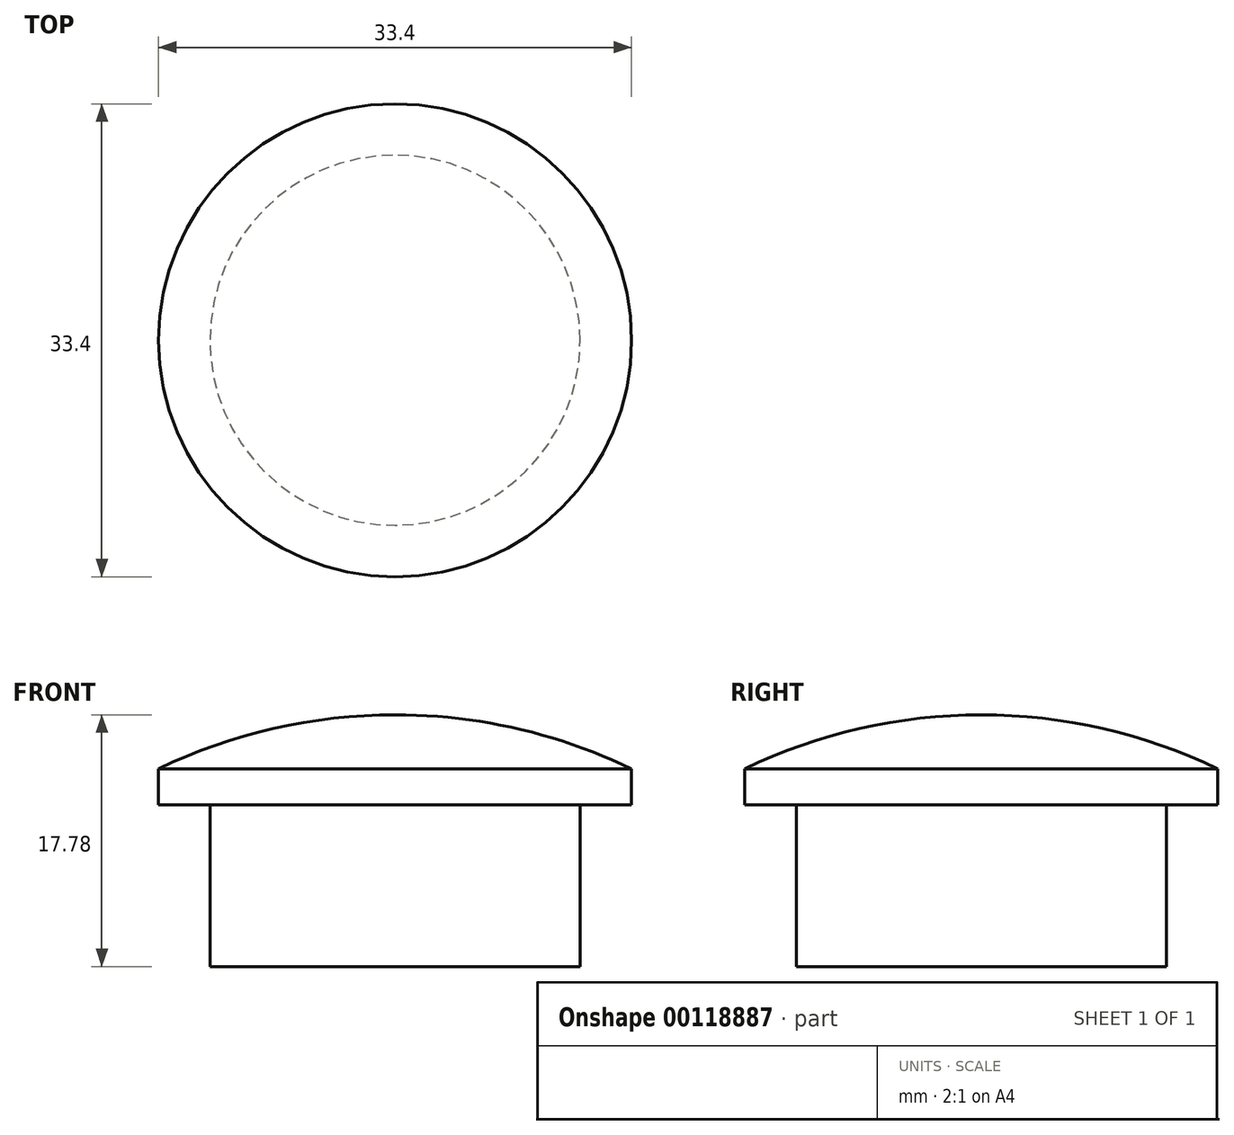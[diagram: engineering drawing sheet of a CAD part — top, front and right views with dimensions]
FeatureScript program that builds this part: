
annotation { "Feature Type Name" : "Feature", "Feature Type Description" : "" }
export const myFeature = defineFeature(function(context is Context, id is Id, definition is map)
    precondition{}
    {
        {
            var Q0;
            Q0=qCreatedBy(makeId("Front.planeOp"),FACE);
            var sketch = newSketch(context, id + "F0", { "sketchPlane" : qUnion([Q0])});
            skLineSegment(sketch, "E0", {"start": v(0, 0) * mm, "end": v(-13.07, 0) * mm});
            skLineSegment(sketch, "E1", {"start": v(-13.07, 0) * mm, "end": v(-13.07, 11.43) * mm});
            skLineSegment(sketch, "E2", {"start": v(-13.07, 11.43) * mm, "end": v(-16.7, 11.43) * mm});
            skLineSegment(sketch, "E3", {"start": v(-16.7, 11.43) * mm, "end": v(-16.7, 13.97) * mm});
            skLineSegment(sketch, "E4", {"start": v(-16.7, 13.97) * mm, "end": v(0, 13.97) * mm});
            skLineSegment(sketch, "E5", {"start": v(0, 13.97) * mm, "end": v(0, 0) * mm});
            skArc(sketch, "E6", {"start": v(0, 17.78) * mm, "mid": v(-8.56, 16.82) * mm, "end": v(-16.7, 13.97) * mm});
            skLineSegment(sketch, "E7", {"start": v(0, 17.78) * mm, "end": v(0, 13.97) * mm});
            skSolve(sketch);
        }
        {
            var Q0;
            Q0=makeQuery(id+"F0.imprint","IMPRINT",FACE,{"disambiguationData":[TD([[makeQuery(id+"F0.imprint","IMPRINT",EDGE,{"derivedFrom":sQuery(id+"F0.wireOp",EDGE,"E0")}),-1.0]])]});
            var Q1;
            Q1=makeQuery(id+"F0.imprint","IMPRINT",FACE,{"disambiguationData":[TD([[makeQuery(id+"F0.imprint","IMPRINT",EDGE,{"derivedFrom":sQuery(id+"F0.wireOp",EDGE,"E4")}),1.0]])]});
            var Q2;
            Q2=sQuery(id+"F0.wireOp",EDGE,"E5");
            revolve(context, id + "F1", {"entities" : qUnion([Q0, Q1]), "axis" : qUnion([Q2]), "revolveType" : RevolveType.FULL});
        }
    });
